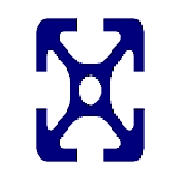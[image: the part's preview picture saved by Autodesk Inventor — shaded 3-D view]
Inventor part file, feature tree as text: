
AUTODESK INVENTOR PART (.ipt)
format: ipt  version: 2020 (Build 240168000, 168)  size: 278,528 bytes
history: native  units: mm
features: other x16, sketch x8, plane x1, split x1
ambient origin geometry x8: Origin, YZ Plane, XZ Plane, XY Plane, X Axis, Y Axis, Z Axis, Center Point
bodies: Body (feature_tree)
feature tree (26):
  other  "Řízená délka"
  other  "Těleso1"
  other  "Start Plane"
  other  "End Plane"
  other  "iFeatureSketch"
  other  "DRAZKA_20:1"
  other  "DRAZKA_20:2"
  other  "DRAZKA_20:3"
  other  "DRAZKA_20:4"
  other  "DIRA_20:1"
  other  "DRAZKA_20:1Axis"
  other  "DRAZKA_20:2Axis"
  other  "DRAZKA_20:3Axis"
  other  "DRAZKA_20:4Axis"
  other  "DIRA_20:1Axis"
  plane  "Work Plane5"
  split  "Split1"
  sketch  "Sketch"  dims[d2=20.0mm d3=20.0mm d4=2.0mm d9=10.0mm d10=100.0mm d11=0.13mm d12=0.0mm d15=0.83mm d16=0.83mm d17=9.8mm d18=3.0mm d19=4.55mm d20=45.0deg d21=5.2mm d22=1.8mm d24=1.0mm d26=0.83mm d27=0.83mm d28=9.8mm d29=3.0mm d30=4.55mm d31=45.0deg d32=5.2mm d33=1.8mm d35=1.0mm d37=0.83mm d38=0.83mm d39=9.8mm d40=3.0mm d41=4.55mm d42=45.0deg d43=5.2mm d44=1.8mm d46=1.0mm d48=0.83mm d49=0.83mm d50=9.8mm d51=3.0mm d52=4.55mm d53=45.0deg d54=5.2mm d55=1.8mm d57=1.0mm d59=4.3mm d60=0.0mm d61=0.0mm d62=0.0mm d63=0.0mm d64=0.0mm d65=0.0mm d66=0.0mm d67=0.0mm d76=90.0deg d14=90.0mm]
  sketch  "Náčrt11"
  other  "Pracovní rovina4"
  sketch  "Náčrt12"
  sketch  "Náčrt6"
  sketch  "Náčrt7"
  sketch  "Náčrt8"
  sketch  "Náčrt9"
  sketch  "Náčrt10"
